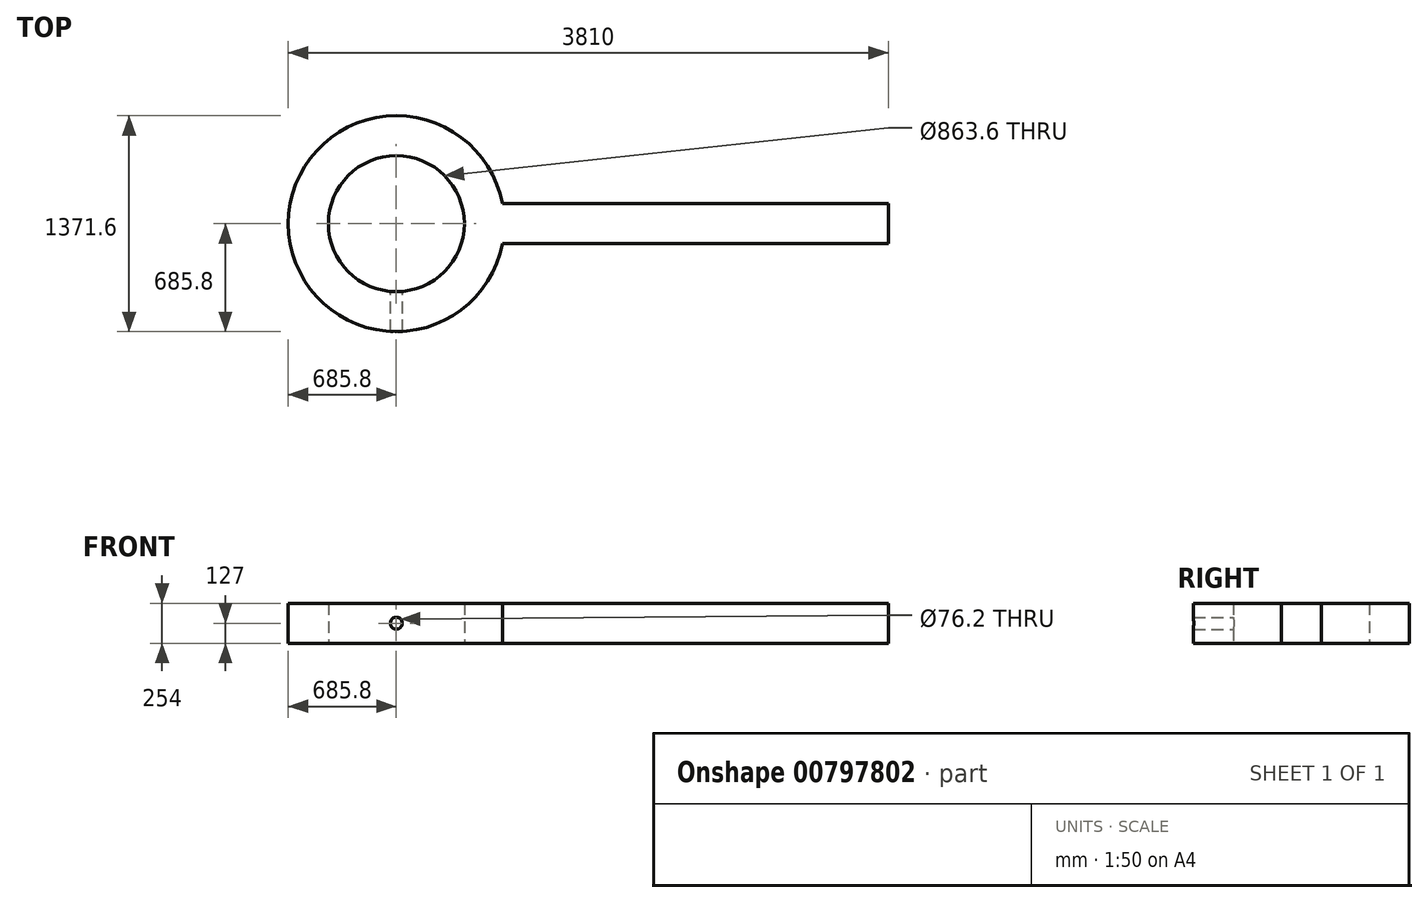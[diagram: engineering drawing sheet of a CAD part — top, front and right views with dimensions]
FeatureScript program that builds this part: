
annotation { "Feature Type Name" : "Feature", "Feature Type Description" : "" }
export const myFeature = defineFeature(function(context is Context, id is Id, definition is map)
    precondition{}
    {
        {
            var Q0;
            Q0=qCreatedBy(makeId("Front.planeOp"),FACE);
            var sketch = newSketch(context, id + "F0", { "sketchPlane" : qUnion([Q0])});
            skLineSegment(sketch, "E0", {"start": v(685.8, 0) * mm, "end": v(685.8, 254) * mm});
            skLineSegment(sketch, "E1", {"start": v(431.8, 0) * mm, "end": v(685.8, 0) * mm});
            skLineSegment(sketch, "E2", {"start": v(685.8, 254) * mm, "end": v(431.8, 254) * mm});
            skLineSegment(sketch, "E3", {"start": v(431.8, 254) * mm, "end": v(431.8, 0) * mm});
            skSolve(sketch);
        }
        {
            var Q0;
            Q0=qCreatedBy(makeId("Front.planeOp"),FACE);
            var sketch = newSketch(context, id + "F1", { "sketchPlane" : qUnion([Q0])});
            skLineSegment(sketch, "E4", {"start": v(0, 0) * mm, "end": v(0, 77.8) * mm});
            skSolve(sketch);
        }
        {
            var Q0;
            Q0=makeQuery(id+"F0.imprint","IMPRINT",FACE,{"disambiguationData":[TD([[makeQuery(id+"F0.imprint","IMPRINT",EDGE,{"derivedFrom":sQuery(id+"F0.wireOp",EDGE,"E0")}),1.0]])]});
            var Q1;
            Q1=sQuery(id+"F1.wireOp",EDGE,"E4");
            revolve(context, id + "F2", {"surfaceOperationType" : NewSurfaceOperationType.NEW, "entities" : qUnion([Q0]), "axis" : qUnion([Q1]), "revolveType" : RevolveType.FULL});
        }
        {
            var Q0;
            Q0=qCreatedBy(makeId("Front.planeOp"),FACE);
            var sketch = newSketch(context, id + "F3", { "sketchPlane" : qUnion([Q0])});
            skLineSegment(sketch, "E5", {"start": v(584.2, 0) * mm, "end": v(3124.2, 0) * mm});
            skLineSegment(sketch, "E6", {"start": v(3124.2, 0) * mm, "end": v(3124.2, 254) * mm});
            skLineSegment(sketch, "E7", {"start": v(3124.2, 254) * mm, "end": v(584.2, 254) * mm});
            skLineSegment(sketch, "E8", {"start": v(584.2, 254) * mm, "end": v(584.2, 0) * mm});
            skSolve(sketch);
        }
        {
            var Q0;
            Q0=makeQuery(id+"F3.imprint","IMPRINT",FACE,{"disambiguationData":[TD([[makeQuery(id+"F3.imprint","IMPRINT",EDGE,{"derivedFrom":sQuery(id+"F3.wireOp",EDGE,"E5")}),1.0]])]});
            extrude(context, id + "F4", {"entities" : qUnion([Q0]), "operationType" : NewBodyOperationType.ADD, "endBound" : BoundingType.SYMMETRIC, "depth" : 254 * mm, "offsetDistance" : 25.4 * mm});
        }
        {
            var Q0;
            Q0=qCreatedBy(makeId("Front.planeOp"),FACE);
            var sketch = newSketch(context, id + "F5", { "sketchPlane" : qUnion([Q0])});
            skLineSegment(sketch, "E9", {"start": v(0, 0) * mm, "end": v(0, 127) * mm});
            skCircle(sketch, "E10", {"center": v(0, 127) * mm, "radius": 38.1 * mm});
            skSolve(sketch);
        }
        {
            var Q0;
            Q0 = qSketchRegion(id + "Fo74p8lPzqzJn6J_1", true);
            var Q1;
            Q1=makeQuery(id+"F5.imprint","IMPRINT",FACE,{"disambiguationData":[TD([[makeQuery(id+"F5.imprint","IMPRINT",EDGE,{"derivedFrom":sQuery(id+"F5.wireOp",EDGE,"E10")}),1.0]])]});
            extrude(context, id + "F6", {"entities" : qUnion([Q0, Q1]), "operationType" : NewBodyOperationType.REMOVE, "endBound" : BoundingType.THROUGH_ALL, "depth" : 25.4 * mm, "offsetDistance" : 25.4 * mm});
        }
    });
